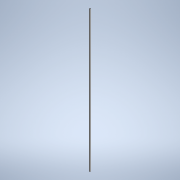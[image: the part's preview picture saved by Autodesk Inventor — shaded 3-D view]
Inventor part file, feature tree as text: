
AUTODESK INVENTOR PART (.ipt)
format: ipt  version: 2022 (Build 260153000, 153)  size: 149,504 bytes
history: native  units: mm
features: extrude x1, sketch x1
ambient origin geometry x8: Origin, YZ Plane, XZ Plane, XY Plane, X Axis, Y Axis, Z Axis, Center Point
bodies: Body1 (feature_tree)
feature tree (2):
  extrude  "Extrusion7"  Depth=5.0mm
  sketch  "Sketch4"  dims[d31=34.456mm d103=5.0mm d104=5.0mm d105=968.0mm d106=0.0mm]
